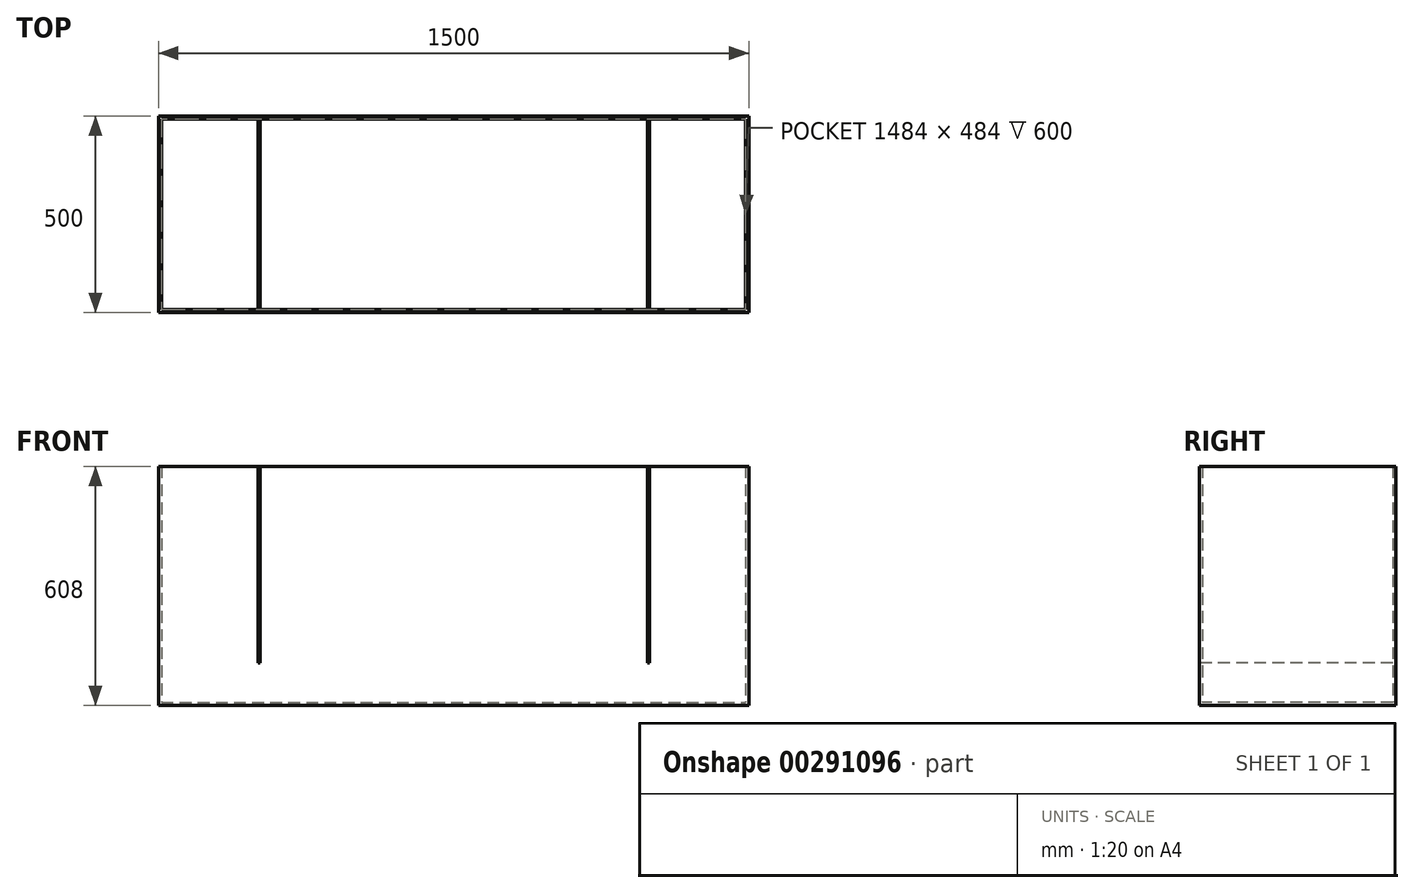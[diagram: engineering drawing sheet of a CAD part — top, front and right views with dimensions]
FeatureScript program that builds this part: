
annotation { "Feature Type Name" : "Feature", "Feature Type Description" : "" }
export const myFeature = defineFeature(function(context is Context, id is Id, definition is map)
    precondition{}
    {
        {
            var Q0;
            Q0=qCreatedBy(makeId("Top.planeOp"),FACE);
            var sketch = newSketch(context, id + "F0", { "sketchPlane" : qUnion([Q0])});
            skLineSegment(sketch, "E0.bottom", {"start": v(-750, 250) * mm, "end": v(750, 250) * mm});
            skLineSegment(sketch, "E0.top", {"start": v(-750, -250) * mm, "end": v(750, -250) * mm});
            skLineSegment(sketch, "E0.left", {"start": v(-750, 250) * mm, "end": v(-750, -250) * mm});
            skLineSegment(sketch, "E0.right", {"start": v(750, 250) * mm, "end": v(750, -250) * mm});
            skPoint(sketch, "E0.middle", {"position": v(0, 0) * mm});
            skLineSegment(sketch, "E1.bottom", {"start": v(-742, 242) * mm, "end": v(742, 242) * mm});
            skLineSegment(sketch, "E1.top", {"start": v(-742, -242) * mm, "end": v(742, -242) * mm});
            skLineSegment(sketch, "E1.left", {"start": v(-742, 242) * mm, "end": v(-742, -242) * mm});
            skLineSegment(sketch, "E1.right", {"start": v(742, 242) * mm, "end": v(742, -242) * mm});
            skSolve(sketch);
        }
        {
            var Q0;
            Q0 = qSketchRegion(id + "F0", true);
            var Q1;
            Q1=makeQuery(id+"F0.imprint","IMPRINT",FACE,{"disambiguationData":[TD([[makeQuery(id+"F0.imprint","IMPRINT",EDGE,{"derivedFrom":sQuery(id+"F0.wireOp",EDGE,"E1.bottom")}),-1.0]])]});
            extrude(context, id + "F1", {"entities" : qUnion([Q0, Q1]), "oppositeDirection" : true, "depth" : 8 * mm});
        }
        {
            var Q0;
            Q0 = qSketchRegion(id + "F0", true);
            extrude(context, id + "F2", {"entities" : qUnion([Q0]), "depth" : 600 * mm});
        }
        {
            var Q0;
            Q0=makeQuery(id+"F1.opExtrude","SWEPT_BODY",BODY,{"disambiguationData":[OSD([sQuery(id+"F0.wireOp",EDGE,"E0.bottom"),sQuery(id+"F0.wireOp",EDGE,"E0.top"),sQuery(id+"F0.wireOp",EDGE,"E0.left"),sQuery(id+"F0.wireOp",EDGE,"E0.right")])]});
            var Q1;
            Q1=makeQuery(id+"F2.opExtrude","SWEPT_BODY",BODY,{"disambiguationData":[OSD([sQuery(id+"F0.wireOp",EDGE,"E0.bottom"),sQuery(id+"F0.wireOp",EDGE,"E0.top"),sQuery(id+"F0.wireOp",EDGE,"E0.left"),sQuery(id+"F0.wireOp",EDGE,"E0.right"),sQuery(id+"F0.wireOp",EDGE,"E1.bottom"),sQuery(id+"F0.wireOp",EDGE,"E1.top"),sQuery(id+"F0.wireOp",EDGE,"E1.left"),sQuery(id+"F0.wireOp",EDGE,"E1.right")])]});
            booleanBodies(context, id + "F3", {"operationType" : BooleanOperationType.UNION, "tools" : qUnion([Q0, Q1])});
        }
        {
            var Q0;
            {var subQ0=sQuery(id+"F0.wireOp",EDGE,"E0.top");Q0=makeQuery(id+"F3.opBoolean","MERGE",FACE,{"derivedFrom":[makeQuery(id+"F1.opExtrude","SWEPT_FACE",FACE,{"disambiguationData":[OSD([subQ0])]}),makeQuery(id+"F2.opExtrude","SWEPT_FACE",FACE,{"disambiguationData":[OSD([subQ0])]})]});}
            var sketch = newSketch(context, id + "F4", { "sketchPlane" : qUnion([Q0])});
            skLineSegment(sketch, "E2.bottom", {"start": v(-497, 600) * mm, "end": v(-492, 600) * mm});
            skLineSegment(sketch, "E2.top", {"start": v(-497, 100) * mm, "end": v(-492, 100) * mm});
            skLineSegment(sketch, "E2.left", {"start": v(-497, 600) * mm, "end": v(-497, 100) * mm});
            skLineSegment(sketch, "E2.right", {"start": v(-492, 600) * mm, "end": v(-492, 100) * mm});
            skLineSegment(sketch, "E3", {"start": v(0, 0) * mm, "end": v(0, 341.46) * mm, "construction": true});
            skLineSegment(sketch, "E4.MirrorCS", {"start": v(497, 600) * mm, "end": v(492, 600) * mm});
            skLineSegment(sketch, "E5.MirrorCS", {"start": v(497, 100) * mm, "end": v(492, 100) * mm});
            skLineSegment(sketch, "E6.MirrorCS", {"start": v(492, 600) * mm, "end": v(492, 100) * mm});
            skLineSegment(sketch, "E7.MirrorCS", {"start": v(497, 600) * mm, "end": v(497, 100) * mm});
            skSolve(sketch);
        }
        {
            var Q0;
            Q0 = qSketchRegion(id + "F4", true);
            var Q1;
            Q1=makeQuery(id+"F2.opExtrude","SWEPT_FACE",FACE,{"disambiguationData":[OSD([sQuery(id+"F0.wireOp",EDGE,"E1.bottom")])]});
            extrude(context, id + "F5", {"entities" : qUnion([Q0]), "endBound" : BoundingType.UP_TO_SURFACE, "oppositeDirection" : true, "endBoundEntityFace" : qUnion([Q1]), "depth" : 25 * mm});
        }
    });
